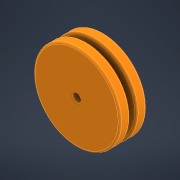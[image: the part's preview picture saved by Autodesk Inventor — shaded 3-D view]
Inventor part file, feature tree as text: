
AUTODESK INVENTOR PART (.ipt)
format: ipt  version: 2021 (Build 250183000, 183)  size: 161,280 bytes
history: native  units: mm
features: fillet x2, revolve x1, sketch x1
ambient origin geometry x8: Origin, YZ Plane, XZ Plane, XY Plane, X Axis, Y Axis, Z Axis, Center Point
bodies: Solid1 (feature_tree)
feature tree (4):
  revolve  "Revolution1"  [1 undecoded]
  fillet  "Fillet1"  Radius=3.5mm
  fillet  "Fillet2"  Radius=7.0mm
  sketch  "Sketch1"  dims[d6=12.0mm d7=12.0mm d10=3.5mm d11=7.0mm d14=90.0deg d15=5.0mm d16=15.0mm d17=50.0mm d18=50.0mm d19=2.0mm d20=2.0mm]
note: 1 required parameter value undecoded (feature->parameter linkage not recoverable at this tier; creation-order binding heuristic only, values carry confidence <= 0.55)
